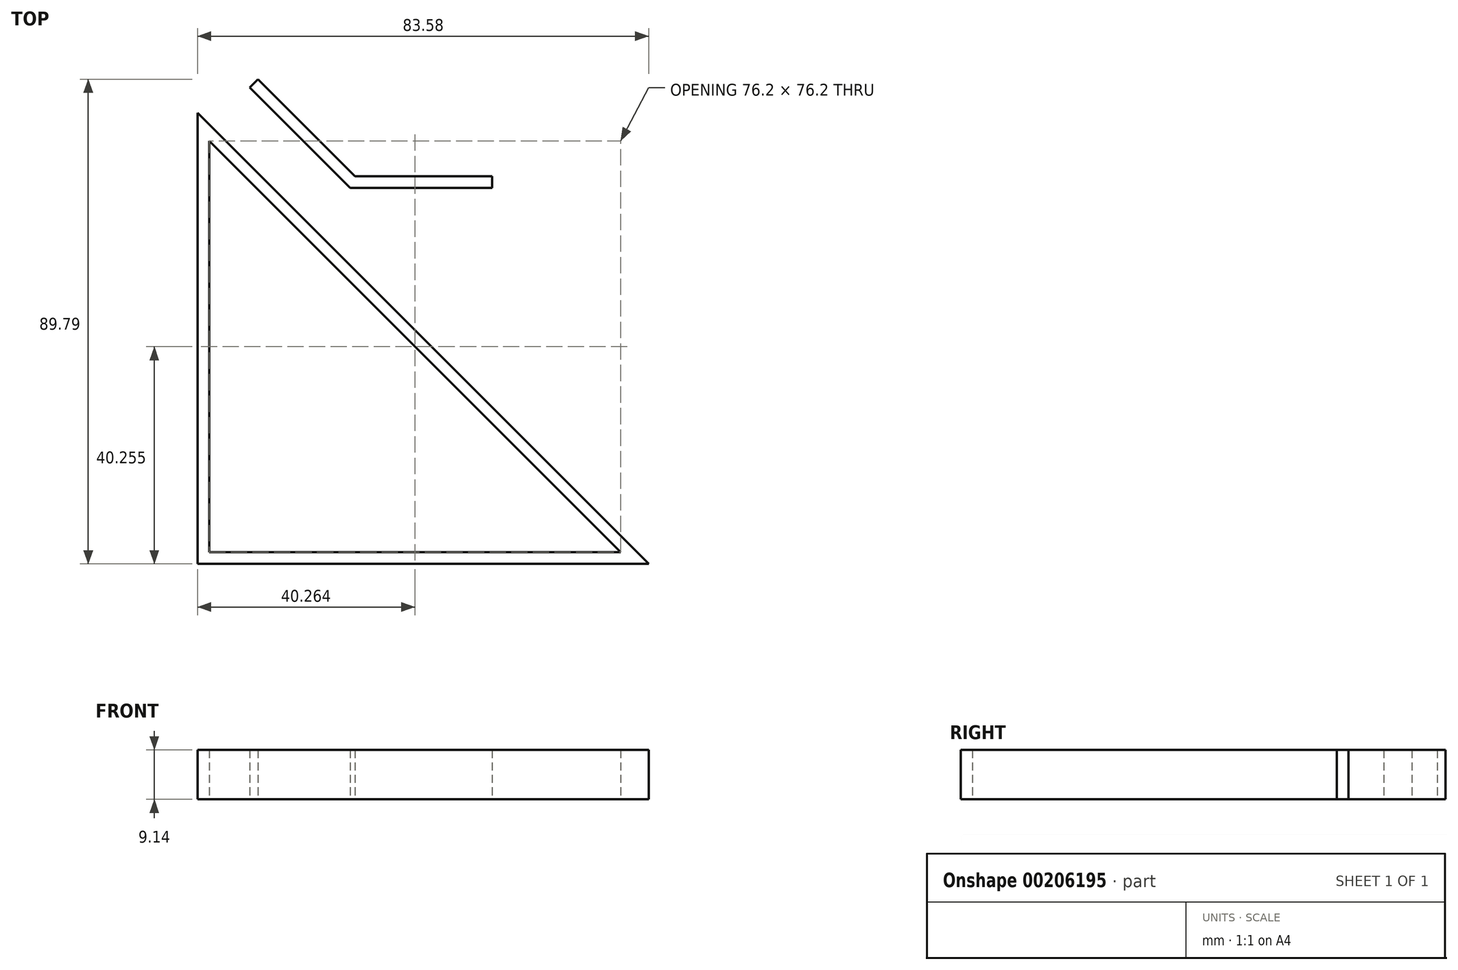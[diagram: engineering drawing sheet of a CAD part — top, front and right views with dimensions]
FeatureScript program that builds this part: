
annotation { "Feature Type Name" : "Feature", "Feature Type Description" : "" }
export const myFeature = defineFeature(function(context is Context, id is Id, definition is map)
    precondition{}
    {
        {
            var Q0;
            Q0=qCreatedBy(makeId("Top.planeOp"),FACE);
            var sketch = newSketch(context, id + "F0", { "sketchPlane" : qUnion([Q0])});
            skLineSegment(sketch, "E0", {"start": v(30.27, 11.82) * mm, "end": v(3.98, 11.82) * mm});
            skLineSegment(sketch, "E1", {"start": v(3.98, 11.82) * mm, "end": v(-14.61, 30.4) * mm});
            skLineSegment(sketch, "E2", {"start": v(-14.61, 30.4) * mm, "end": v(-13.09, 31.94) * mm});
            skLineSegment(sketch, "E3", {"start": v(-13.09, 31.94) * mm, "end": v(4.87, 13.98) * mm});
            skLineSegment(sketch, "E4", {"start": v(4.87, 13.98) * mm, "end": v(30.27, 13.98) * mm});
            skLineSegment(sketch, "E5", {"start": v(30.27, 13.98) * mm, "end": v(30.27, 11.82) * mm});
            skLineSegment(sketch, "E6", {"start": v(3.98, 11.82) * mm, "end": v(4.87, 13.98) * mm, "construction": true});
            skLineSegment(sketch, "E7", {"start": v(59.29, -57.85) * mm, "end": v(-24.29, 25.72) * mm});
            skLineSegment(sketch, "E8", {"start": v(-22.13, -55.7) * mm, "end": v(54.07, -55.7) * mm});
            skLineSegment(sketch, "E9", {"start": v(-24.29, -55.7) * mm, "end": v(-24.29, 25.72) * mm});
            skLineSegment(sketch, "E10", {"start": v(54.07, -55.7) * mm, "end": v(-22.13, 20.5) * mm});
            skLineSegment(sketch, "E11", {"start": v(-22.13, 20.5) * mm, "end": v(-22.13, -55.7) * mm});
            skLineSegment(sketch, "E12", {"start": v(59.29, -57.85) * mm, "end": v(-24.29, -57.85) * mm});
            skLineSegment(sketch, "E13", {"start": v(-24.29, -57.85) * mm, "end": v(-24.29, -55.7) * mm});
            skSolve(sketch);
        }
        {
            var Q0;
            Q0=qSketchRegion(id+"F0",true);
            extrude(context, id + "F1", {"entities" : qUnion([Q0]), "depth" : 9.14 * mm});
        }
    });
